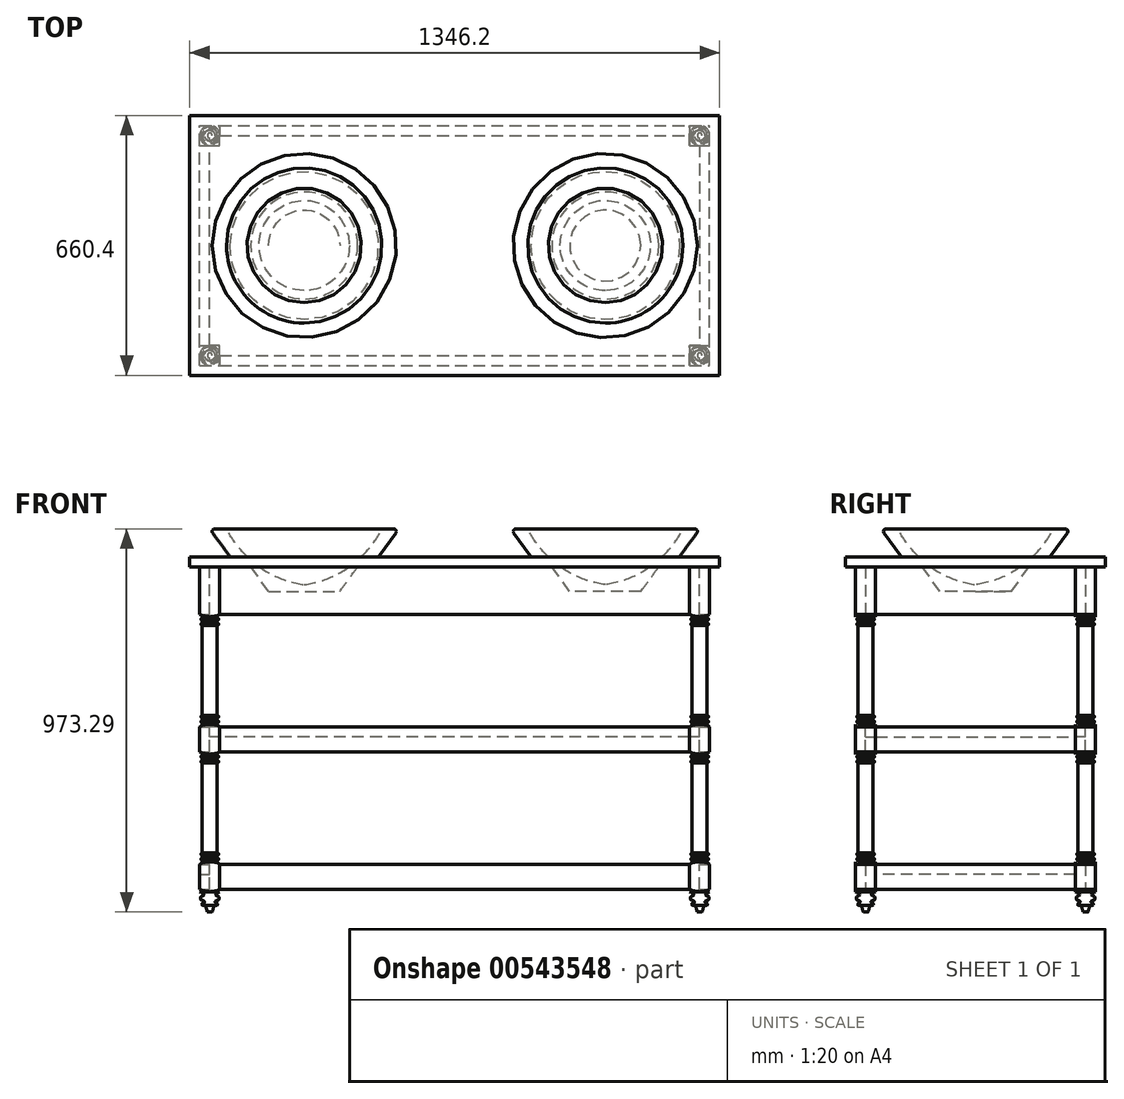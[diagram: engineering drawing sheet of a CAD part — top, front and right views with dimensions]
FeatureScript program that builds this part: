
annotation { "Feature Type Name" : "Feature", "Feature Type Description" : "" }
export const myFeature = defineFeature(function(context is Context, id is Id, definition is map)
    precondition{}
    {
        {
            var Q0;
            Q0=qCreatedBy(makeId("Front.planeOp"),FACE);
            var sketch = newSketch(context, id + "F0", { "sketchPlane" : qUnion([Q0])});
            skLineSegment(sketch, "E0", {"start": v(-464.69, 397.34) * mm, "end": v(-413.89, 397.34) * mm});
            skLineSegment(sketch, "E1", {"start": v(-464.69, 270.34) * mm, "end": v(-413.89, 270.34) * mm});
            skArc(sketch, "E2", {"start": v(-464.69, 276.7) * mm, "mid": v(-439.29, 270.34) * mm, "end": v(-413.89, 276.7) * mm});
            skArc(sketch, "E3", {"start": v(-458.34, 267.17) * mm, "mid": v(-461.51, 264) * mm, "end": v(-458.34, 260.82) * mm});
            skArc(sketch, "E4", {"start": v(-420.24, 260.82) * mm, "mid": v(-417.06, 264) * mm, "end": v(-420.24, 267.17) * mm});
            skArc(sketch, "E5", {"start": v(-458.34, 254.47) * mm, "mid": v(-461.51, 251.3) * mm, "end": v(-458.34, 248.12) * mm});
            skArc(sketch, "E6", {"start": v(-420.24, 248.12) * mm, "mid": v(-417.06, 251.3) * mm, "end": v(-420.24, 254.47) * mm});
            skLineSegment(sketch, "E7", {"start": v(-458.34, 267.17) * mm, "end": v(-458.34, 270.34) * mm});
            skLineSegment(sketch, "E8", {"start": v(-458.34, 260.82) * mm, "end": v(-458.34, 254.47) * mm});
            skLineSegment(sketch, "E9", {"start": v(-420.24, 267.17) * mm, "end": v(-420.24, 270.34) * mm});
            skLineSegment(sketch, "E10", {"start": v(-420.24, 260.82) * mm, "end": v(-420.24, 254.47) * mm});
            skLineSegment(sketch, "E11", {"start": v(-464.69, -2.7) * mm, "end": v(-413.89, -2.7) * mm});
            skArc(sketch, "E12", {"start": v(-413.89, -9.06) * mm, "mid": v(-439.29, -2.7) * mm, "end": v(-464.69, -9.06) * mm});
            skArc(sketch, "E13", {"start": v(-458.34, 6.82) * mm, "mid": v(-461.51, 3.64) * mm, "end": v(-458.34, 0.47) * mm});
            skArc(sketch, "E14", {"start": v(-420.24, 0.47) * mm, "mid": v(-417.06, 3.64) * mm, "end": v(-420.24, 6.82) * mm});
            skArc(sketch, "E15", {"start": v(-458.34, 19.52) * mm, "mid": v(-461.51, 16.34) * mm, "end": v(-458.34, 13.17) * mm});
            skArc(sketch, "E16", {"start": v(-420.24, 13.17) * mm, "mid": v(-417.06, 16.34) * mm, "end": v(-420.24, 19.52) * mm});
            skLineSegment(sketch, "E17", {"start": v(-458.34, 0.47) * mm, "end": v(-458.34, -2.7) * mm});
            skLineSegment(sketch, "E18", {"start": v(-458.34, 6.82) * mm, "end": v(-458.34, 13.17) * mm});
            skLineSegment(sketch, "E19", {"start": v(-420.24, 0.47) * mm, "end": v(-420.24, -2.7) * mm});
            skLineSegment(sketch, "E20", {"start": v(-420.24, 6.82) * mm, "end": v(-420.24, 13.17) * mm});
            skLineSegment(sketch, "E21", {"start": v(-458.34, 248.12) * mm, "end": v(-458.34, 19.52) * mm});
            skLineSegment(sketch, "E22", {"start": v(-420.24, 248.12) * mm, "end": v(-420.24, 19.52) * mm});
            skLineSegment(sketch, "E23", {"start": v(-464.69, -78.9) * mm, "end": v(-413.89, -78.9) * mm});
            skLineSegment(sketch, "E24", {"start": v(-464.69, -78.9) * mm, "end": v(-464.69, -2.7) * mm});
            skLineSegment(sketch, "E25", {"start": v(-413.89, -2.7) * mm, "end": v(-413.89, -78.9) * mm});
            skArc(sketch, "E26", {"start": v(-464.69, -72.56) * mm, "mid": v(-439.29, -78.9) * mm, "end": v(-413.89, -72.56) * mm});
            skArc(sketch, "E27", {"start": v(-458.34, -342.43) * mm, "mid": v(-461.51, -345.6) * mm, "end": v(-458.34, -348.78) * mm});
            skArc(sketch, "E28", {"start": v(-420.24, -348.78) * mm, "mid": v(-417.06, -345.6) * mm, "end": v(-420.24, -342.43) * mm});
            skArc(sketch, "E29", {"start": v(-458.34, -329.73) * mm, "mid": v(-461.51, -332.9) * mm, "end": v(-458.34, -336.08) * mm});
            skArc(sketch, "E30", {"start": v(-420.24, -336.08) * mm, "mid": v(-417.06, -332.9) * mm, "end": v(-420.24, -329.73) * mm});
            skLineSegment(sketch, "E31", {"start": v(-458.34, -342.43) * mm, "end": v(-458.34, -336.08) * mm});
            skLineSegment(sketch, "E32", {"start": v(-420.24, -342.43) * mm, "end": v(-420.24, -336.08) * mm});
            skArc(sketch, "E33", {"start": v(-458.34, -82.08) * mm, "mid": v(-461.51, -85.26) * mm, "end": v(-458.34, -88.43) * mm});
            skArc(sketch, "E34", {"start": v(-420.24, -88.43) * mm, "mid": v(-417.06, -85.26) * mm, "end": v(-420.24, -82.08) * mm});
            skArc(sketch, "E35", {"start": v(-458.34, -94.78) * mm, "mid": v(-461.51, -97.96) * mm, "end": v(-458.34, -101.13) * mm});
            skArc(sketch, "E36", {"start": v(-420.24, -101.13) * mm, "mid": v(-417.06, -97.96) * mm, "end": v(-420.24, -94.78) * mm});
            skLineSegment(sketch, "E37", {"start": v(-458.34, -88.43) * mm, "end": v(-458.34, -94.78) * mm});
            skLineSegment(sketch, "E38", {"start": v(-420.24, -88.43) * mm, "end": v(-420.24, -94.78) * mm});
            skLineSegment(sketch, "E39", {"start": v(-458.34, -329.73) * mm, "end": v(-458.34, -101.13) * mm});
            skLineSegment(sketch, "E40", {"start": v(-420.24, -329.73) * mm, "end": v(-420.24, -101.13) * mm});
            skLineSegment(sketch, "E41", {"start": v(-413.89, 397.34) * mm, "end": v(-413.89, 270.34) * mm});
            skLineSegment(sketch, "E42", {"start": v(-464.69, 270.34) * mm, "end": v(-464.69, 397.34) * mm});
            skLineSegment(sketch, "E43", {"start": v(-458.34, -82.08) * mm, "end": v(-458.34, -78.9) * mm});
            skLineSegment(sketch, "E44", {"start": v(-420.24, -82.08) * mm, "end": v(-420.24, -78.9) * mm});
            skLineSegment(sketch, "E45", {"start": v(-464.69, -428.16) * mm, "end": v(-413.89, -428.16) * mm});
            skArc(sketch, "E46", {"start": v(-464.69, -421.8) * mm, "mid": v(-439.29, -428.16) * mm, "end": v(-413.89, -421.8) * mm});
            skLineSegment(sketch, "E47", {"start": v(-464.69, -351.96) * mm, "end": v(-413.89, -351.96) * mm});
            skLineSegment(sketch, "E48", {"start": v(-464.69, -351.96) * mm, "end": v(-464.69, -428.16) * mm});
            skLineSegment(sketch, "E49", {"start": v(-413.89, -428.16) * mm, "end": v(-413.89, -351.96) * mm});
            skArc(sketch, "E50", {"start": v(-413.89, -358.3) * mm, "mid": v(-439.29, -351.96) * mm, "end": v(-464.69, -358.3) * mm});
            skLineSegment(sketch, "E51", {"start": v(-458.34, -348.78) * mm, "end": v(-458.34, -351.96) * mm});
            skLineSegment(sketch, "E52", {"start": v(-420.24, -348.78) * mm, "end": v(-420.24, -351.96) * mm});
            skFitSpline(sketch, "E53", {"points": [v(-464.69, -428.16) * mm, v(-457.34, -432.47) * mm, v(-454.04, -435.15) * mm, v(-455.28, -437.83) * mm, v(-459.6, -439.69) * mm, v(-462.5, -441.75) * mm, v(-463.11, -444.43) * mm, v(-462.7, -448.14) * mm, v(-460.02, -449.79) * mm, v(-456.72, -451.03) * mm, v(-454.66, -451.44) * mm, v(-452.6, -454.94) * mm, v(-455.9, -457.21) * mm, v(-459.2, -458.86) * mm, v(-459.4, -461.34) * mm, v(-457.54, -462.37) * mm, v(-455.9, -462.57) * mm, v(-453, -462.99) * mm]});
            skFitSpline(sketch, "E54", {"points": [v(-413.89, -428.16) * mm, v(-421.23, -432.47) * mm, v(-424.53, -435.15) * mm, v(-423.3, -437.83) * mm, v(-418.97, -439.69) * mm, v(-416.08, -441.75) * mm, v(-415.46, -444.43) * mm, v(-415.87, -448.14) * mm, v(-418.55, -449.79) * mm, v(-421.85, -451.03) * mm, v(-423.91, -451.44) * mm, v(-425.98, -454.94) * mm, v(-422.68, -457.21) * mm, v(-419.38, -458.86) * mm, v(-419.17, -461.34) * mm, v(-421.03, -462.37) * mm, v(-422.68, -462.57) * mm, v(-425.56, -462.99) * mm]});
            skLineSegment(sketch, "E55", {"start": v(-445.58, -479.9) * mm, "end": v(-432.99, -479.9) * mm});
            skLineSegment(sketch, "E56", {"start": v(779.91, 397.34) * mm, "end": v(830.71, 397.34) * mm});
            skLineSegment(sketch, "E57", {"start": v(779.91, 270.34) * mm, "end": v(830.71, 270.34) * mm});
            skArc(sketch, "E58", {"start": v(779.91, 276.7) * mm, "mid": v(805.31, 270.34) * mm, "end": v(830.71, 276.7) * mm});
            skArc(sketch, "E59", {"start": v(786.26, 267.17) * mm, "mid": v(783.09, 264) * mm, "end": v(786.26, 260.82) * mm});
            skArc(sketch, "E60", {"start": v(824.36, 260.82) * mm, "mid": v(827.54, 264) * mm, "end": v(824.36, 267.17) * mm});
            skArc(sketch, "E61", {"start": v(786.26, 254.47) * mm, "mid": v(783.09, 251.3) * mm, "end": v(786.26, 248.12) * mm});
            skArc(sketch, "E62", {"start": v(824.36, 248.12) * mm, "mid": v(827.54, 251.3) * mm, "end": v(824.36, 254.47) * mm});
            skLineSegment(sketch, "E63", {"start": v(786.26, 267.17) * mm, "end": v(786.26, 270.34) * mm});
            skLineSegment(sketch, "E64", {"start": v(786.26, 260.82) * mm, "end": v(786.26, 254.47) * mm});
            skLineSegment(sketch, "E65", {"start": v(824.36, 267.17) * mm, "end": v(824.36, 270.34) * mm});
            skLineSegment(sketch, "E66", {"start": v(824.36, 260.82) * mm, "end": v(824.36, 254.47) * mm});
            skLineSegment(sketch, "E67", {"start": v(779.91, -2.7) * mm, "end": v(830.71, -2.7) * mm});
            skArc(sketch, "E68", {"start": v(830.71, -9.06) * mm, "mid": v(805.31, -2.7) * mm, "end": v(779.91, -9.06) * mm});
            skArc(sketch, "E69", {"start": v(786.26, 6.82) * mm, "mid": v(783.09, 3.64) * mm, "end": v(786.26, 0.47) * mm});
            skArc(sketch, "E70", {"start": v(824.36, 0.47) * mm, "mid": v(827.54, 3.64) * mm, "end": v(824.36, 6.82) * mm});
            skArc(sketch, "E71", {"start": v(786.26, 19.52) * mm, "mid": v(783.09, 16.34) * mm, "end": v(786.26, 13.17) * mm});
            skArc(sketch, "E72", {"start": v(824.36, 13.17) * mm, "mid": v(827.54, 16.34) * mm, "end": v(824.36, 19.52) * mm});
            skLineSegment(sketch, "E73", {"start": v(786.26, 0.47) * mm, "end": v(786.26, -2.7) * mm});
            skLineSegment(sketch, "E74", {"start": v(786.26, 6.82) * mm, "end": v(786.26, 13.17) * mm});
            skLineSegment(sketch, "E75", {"start": v(824.36, 0.47) * mm, "end": v(824.36, -2.7) * mm});
            skLineSegment(sketch, "E76", {"start": v(824.36, 6.82) * mm, "end": v(824.36, 13.17) * mm});
            skLineSegment(sketch, "E77", {"start": v(786.26, 248.12) * mm, "end": v(786.26, 19.52) * mm});
            skLineSegment(sketch, "E78", {"start": v(824.36, 248.12) * mm, "end": v(824.36, 19.52) * mm});
            skLineSegment(sketch, "E79", {"start": v(779.91, -78.9) * mm, "end": v(830.71, -78.9) * mm});
            skLineSegment(sketch, "E80", {"start": v(779.91, -78.9) * mm, "end": v(779.91, -2.7) * mm});
            skLineSegment(sketch, "E81", {"start": v(830.71, -2.7) * mm, "end": v(830.71, -78.9) * mm});
            skArc(sketch, "E82", {"start": v(779.91, -72.56) * mm, "mid": v(805.31, -78.9) * mm, "end": v(830.71, -72.56) * mm});
            skArc(sketch, "E83", {"start": v(786.26, -342.43) * mm, "mid": v(783.09, -345.6) * mm, "end": v(786.26, -348.78) * mm});
            skArc(sketch, "E84", {"start": v(824.36, -348.78) * mm, "mid": v(827.54, -345.6) * mm, "end": v(824.36, -342.43) * mm});
            skArc(sketch, "E85", {"start": v(786.26, -329.73) * mm, "mid": v(783.09, -332.9) * mm, "end": v(786.26, -336.08) * mm});
            skArc(sketch, "E86", {"start": v(824.36, -336.08) * mm, "mid": v(827.54, -332.9) * mm, "end": v(824.36, -329.73) * mm});
            skLineSegment(sketch, "E87", {"start": v(786.26, -342.43) * mm, "end": v(786.26, -336.08) * mm});
            skLineSegment(sketch, "E88", {"start": v(824.36, -342.43) * mm, "end": v(824.36, -336.08) * mm});
            skArc(sketch, "E89", {"start": v(786.26, -82.08) * mm, "mid": v(783.09, -85.26) * mm, "end": v(786.26, -88.43) * mm});
            skArc(sketch, "E90", {"start": v(824.36, -88.43) * mm, "mid": v(827.54, -85.26) * mm, "end": v(824.36, -82.08) * mm});
            skArc(sketch, "E91", {"start": v(786.26, -94.78) * mm, "mid": v(783.09, -97.96) * mm, "end": v(786.26, -101.13) * mm});
            skArc(sketch, "E92", {"start": v(824.36, -101.13) * mm, "mid": v(827.54, -97.96) * mm, "end": v(824.36, -94.78) * mm});
            skLineSegment(sketch, "E93", {"start": v(786.26, -88.43) * mm, "end": v(786.26, -94.78) * mm});
            skLineSegment(sketch, "E94", {"start": v(824.36, -88.43) * mm, "end": v(824.36, -94.78) * mm});
            skLineSegment(sketch, "E95", {"start": v(786.26, -329.73) * mm, "end": v(786.26, -101.13) * mm});
            skLineSegment(sketch, "E96", {"start": v(824.36, -329.73) * mm, "end": v(824.36, -101.13) * mm});
            skLineSegment(sketch, "E97", {"start": v(830.71, 397.34) * mm, "end": v(830.71, 270.34) * mm});
            skLineSegment(sketch, "E98", {"start": v(779.91, 270.34) * mm, "end": v(779.91, 397.34) * mm});
            skLineSegment(sketch, "E99", {"start": v(786.26, -82.08) * mm, "end": v(786.26, -78.9) * mm});
            skLineSegment(sketch, "E100", {"start": v(824.36, -82.08) * mm, "end": v(824.36, -78.9) * mm});
            skLineSegment(sketch, "E101", {"start": v(805.31, -428.16) * mm, "end": v(779.91, -428.16) * mm});
            skArc(sketch, "E102", {"start": v(779.91, -421.8) * mm, "mid": v(805.31, -428.16) * mm, "end": v(830.71, -421.8) * mm});
            skLineSegment(sketch, "E103", {"start": v(779.91, -351.96) * mm, "end": v(830.71, -351.96) * mm});
            skLineSegment(sketch, "E104", {"start": v(779.91, -351.96) * mm, "end": v(779.91, -428.16) * mm});
            skLineSegment(sketch, "E105", {"start": v(830.71, -428.16) * mm, "end": v(830.71, -351.96) * mm});
            skArc(sketch, "E106", {"start": v(830.71, -358.3) * mm, "mid": v(805.31, -351.96) * mm, "end": v(779.91, -358.3) * mm});
            skLineSegment(sketch, "E107", {"start": v(786.26, -348.78) * mm, "end": v(786.26, -351.96) * mm});
            skLineSegment(sketch, "E108", {"start": v(824.36, -348.78) * mm, "end": v(824.36, -351.96) * mm});
            skFitSpline(sketch, "E109", {"points": [v(779.91, -428.16) * mm, v(787.26, -432.47) * mm, v(790.56, -435.15) * mm, v(789.32, -437.83) * mm, v(785, -439.69) * mm, v(782.1, -441.75) * mm, v(781.49, -444.43) * mm, v(781.9, -448.14) * mm, v(784.58, -449.79) * mm, v(787.88, -451.03) * mm, v(789.94, -451.44) * mm, v(792, -454.94) * mm, v(788.7, -457.21) * mm, v(785.4, -458.86) * mm, v(785.2, -461.34) * mm, v(787.06, -462.37) * mm, v(788.7, -462.57) * mm, v(791.6, -462.99) * mm]});
            skFitSpline(sketch, "E110", {"points": [v(830.71, -428.16) * mm, v(823.37, -432.47) * mm, v(820.07, -435.15) * mm, v(821.3, -437.83) * mm, v(825.63, -439.69) * mm, v(828.52, -441.75) * mm, v(829.14, -444.43) * mm, v(828.73, -448.14) * mm, v(826.05, -449.79) * mm, v(822.75, -451.03) * mm, v(820.69, -451.44) * mm, v(818.62, -454.94) * mm, v(821.92, -457.21) * mm, v(825.22, -458.86) * mm, v(825.43, -461.34) * mm, v(823.57, -462.37) * mm, v(821.92, -462.57) * mm, v(819.04, -462.99) * mm]});
            skFitSpline(sketch, "E111", {"points": [v(-425.56, -462.99) * mm, v(-428.05, -464.67) * mm, v(-432.99, -479.9) * mm], "startDerivative": vector(-8.41, -3.1) * mm, "endDerivative": vector(-6.66, -27.5) * mm});
            skFitSpline(sketch, "E112.MirrorCS", {"points": [v(-453, -462.99) * mm, v(-450.52, -464.67) * mm, v(-445.58, -479.9) * mm], "startDerivative": vector(8.41, -3.1) * mm, "endDerivative": vector(6.66, -27.5) * mm});
            skLineSegment(sketch, "E113", {"start": v(-413.89, 397.34) * mm, "end": v(779.91, 397.34) * mm});
            skLineSegment(sketch, "E114", {"start": v(183.01, 397.34) * mm, "end": v(183.01, 64.11) * mm});
            skFitSpline(sketch, "E115.MirrorCS", {"points": [v(791.6, -462.99) * mm, v(794.08, -464.67) * mm, v(799.02, -479.9) * mm], "startDerivative": vector(8.41, -3.1) * mm, "endDerivative": vector(6.66, -27.5) * mm});
            skFitSpline(sketch, "E116.MirrorCS", {"points": [v(819.04, -462.99) * mm, v(816.55, -464.67) * mm, v(811.61, -479.9) * mm], "startDerivative": vector(-8.41, -3.1) * mm, "endDerivative": vector(-6.66, -27.5) * mm});
            skLineSegment(sketch, "E117", {"start": v(799.02, -479.9) * mm, "end": v(805.31, -479.9) * mm});
            skLineSegment(sketch, "E118", {"start": v(805.31, -428.16) * mm, "end": v(805.31, -479.9) * mm});
            skLineSegment(sketch, "E119", {"start": v(-439.29, -428.16) * mm, "end": v(-439.29, -479.9) * mm});
            skLineSegment(sketch, "E120", {"start": v(-439.29, -78.9) * mm, "end": v(-439.29, -351.96) * mm});
            skLineSegment(sketch, "E121", {"start": v(-439.29, 270.34) * mm, "end": v(-439.29, -2.7) * mm});
            skLineSegment(sketch, "E122", {"start": v(805.31, 270.34) * mm, "end": v(805.31, -2.7) * mm});
            skLineSegment(sketch, "E123", {"start": v(805.31, -78.9) * mm, "end": v(805.31, -351.96) * mm});
            skSolve(sketch);
        }
        {
            var Q0;
            {var subQ1=sQuery(id+"F0.wireOp",EDGE,"E0");Q0=makeQuery(id+"F0.imprint","IMPRINT",FACE,{"disambiguationData":[TD([[makeQuery(id+"F0.imprint","IMPRINT",EDGE,{"derivedFrom":subQ1}),-1.0]])]});}
            extrude(context, id + "F1", {"entities" : qUnion([Q0]), "endBound" : BoundingType.SYMMETRIC, "depth" : 50.8 * mm, "offsetDistance" : 25.4 * mm});
        }
        {
            var Q0;
            {var subQ1=sQuery(id+"F0.wireOp",EDGE,"E56");Q0=makeQuery(id+"F0.imprint","IMPRINT",FACE,{"disambiguationData":[TD([[makeQuery(id+"F0.imprint","IMPRINT",EDGE,{"derivedFrom":subQ1}),-1.0]])]});}
            var Q1;
            {var subQ1=sQuery(id+"F0.wireOp",EDGE,"E12");var subQ6=sQuery(id+"F0.wireOp",EDGE,"E25");var subQ9=makeQuery(id+"F0.imprint","INTERSECT",VERTEX,{"derivedFrom":[subQ1,subQ6]});Q1=makeQuery(id+"F0.imprint","IMPRINT",FACE,{"disambiguationData":[TD([[makeQuery(id+"F0.imprint","IMPRINT",EDGE,{"disambiguationData":[TD([[subQ9,-1.0]])],"derivedFrom":subQ1}),1.0]])]});}
            var Q2;
            {var subQ1=sQuery(id+"F0.wireOp",EDGE,"E68");var subQ6=sQuery(id+"F0.wireOp",EDGE,"E81");var subQ9=makeQuery(id+"F0.imprint","INTERSECT",VERTEX,{"derivedFrom":[subQ1,subQ6]});Q2=makeQuery(id+"F0.imprint","IMPRINT",FACE,{"disambiguationData":[TD([[makeQuery(id+"F0.imprint","IMPRINT",EDGE,{"disambiguationData":[TD([[subQ9,-1.0]])],"derivedFrom":subQ1}),1.0]])]});}
            var Q3;
            {var subQ0=sQuery(id+"F0.wireOp",EDGE,"E48");var subQ1=sQuery(id+"F0.wireOp",EDGE,"E46");var subQ2=makeQuery(id+"F0.imprint","INTERSECT",VERTEX,{"derivedFrom":[subQ1,subQ0]});Q3=makeQuery(id+"F0.imprint","IMPRINT",FACE,{"disambiguationData":[TD([[makeQuery(id+"F0.imprint","IMPRINT",EDGE,{"disambiguationData":[TD([[subQ2,-1.0]])],"derivedFrom":subQ1}),1.0]])]});}
            var Q4;
            {var subQ0=sQuery(id+"F0.wireOp",EDGE,"E104");var subQ1=sQuery(id+"F0.wireOp",EDGE,"E102");var subQ2=makeQuery(id+"F0.imprint","INTERSECT",VERTEX,{"derivedFrom":[subQ1,subQ0]});Q4=makeQuery(id+"F0.imprint","IMPRINT",FACE,{"disambiguationData":[TD([[makeQuery(id+"F0.imprint","IMPRINT",EDGE,{"disambiguationData":[TD([[subQ2,-1.0]])],"derivedFrom":subQ1}),1.0]])]});}
            extrude(context, id + "F2", {"entities" : qUnion([Q0, Q1, Q2, Q3, Q4]), "endBound" : BoundingType.SYMMETRIC, "depth" : 50.8 * mm, "offsetDistance" : 25.4 * mm});
        }
        {
            var Q0;
            Q0=makeQuery(id+"F0.imprint","IMPRINT",FACE,{"disambiguationData":[TD([[makeQuery(id+"F0.imprint","IMPRINT",EDGE,{"derivedFrom":sQuery(id+"F0.wireOp",EDGE,"E27")}),1.0]])]});
            var Q1;
            Q1=makeQuery(id+"F0.imprint","IMPRINT",FACE,{"disambiguationData":[TD([[makeQuery(id+"F0.imprint","IMPRINT",EDGE,{"derivedFrom":sQuery(id+"F0.wireOp",EDGE,"E3")}),1.0]])]});
            var Q2;
            Q2=sQuery(id+"F0.wireOp",EDGE,"E120");
            revolve(context, id + "F3", {"entities" : qUnion([Q0, Q1]), "axis" : qUnion([Q2]), "revolveType" : RevolveType.FULL});
        }
        {
            var Q0;
            {var subQ1=sQuery(id+"F0.wireOp",EDGE,"E53");Q0=makeQuery(id+"F0.imprint","IMPRINT",FACE,{"disambiguationData":[TD([[makeQuery(id+"F0.imprint","IMPRINT",EDGE,{"derivedFrom":subQ1}),1.0]])]});}
            var Q1;
            Q1=sQuery(id+"F0.wireOp",EDGE,"E119");
            revolve(context, id + "F4", {"operationType" : NewBodyOperationType.ADD, "entities" : qUnion([Q0]), "axis" : qUnion([Q1]), "revolveType" : RevolveType.FULL});
        }
        {
            var Q0;
            Q0=makeQuery(id+"F0.imprint","IMPRINT",FACE,{"disambiguationData":[TD([[makeQuery(id+"F0.imprint","IMPRINT",EDGE,{"derivedFrom":sQuery(id+"F0.wireOp",EDGE,"E59")}),1.0]])]});
            var Q1;
            Q1=makeQuery(id+"F0.imprint","IMPRINT",FACE,{"disambiguationData":[TD([[makeQuery(id+"F0.imprint","IMPRINT",EDGE,{"derivedFrom":sQuery(id+"F0.wireOp",EDGE,"E83")}),1.0]])]});
            var Q2;
            Q2=sQuery(id+"F0.wireOp",EDGE,"E122");
            revolve(context, id + "F5", {"entities" : qUnion([Q0, Q1]), "axis" : qUnion([Q2]), "revolveType" : RevolveType.FULL});
        }
        {
            var Q0;
            Q0=makeQuery(id+"F0.imprint","IMPRINT",FACE,{"disambiguationData":[TD([[makeQuery(id+"F0.imprint","IMPRINT",EDGE,{"derivedFrom":sQuery(id+"F0.wireOp",EDGE,"E101")}),1.0]])]});
            var Q1;
            Q1=sQuery(id+"F0.wireOp",EDGE,"E123");
            revolve(context, id + "F6", {"operationType" : NewBodyOperationType.ADD, "entities" : qUnion([Q0]), "axis" : qUnion([Q1]), "revolveType" : RevolveType.FULL});
        }
        {
            var Q0;
            Q0=qCreatedBy(makeId("Front.planeOp"),FACE);
            cPlane(context, id + "F7", {"entities" : qUnion([Q0]), "cplaneType" : CPlaneType.OFFSET, "offset" : 25.4 * mm, "width" : 152.4 * mm, "height" : 152.4 * mm});
        }
        {
            var Q0;
            Q0=qCreatedBy(id+"F7.planeOp",FACE);
            var sketch = newSketch(context, id + "F8", { "sketchPlane" : qUnion([Q0])});
            skLineSegment(sketch, "E124.0.0", {"start": v(-464.69, 397.34) * mm, "end": v(-464.69, 276.7) * mm});
            skArc(sketch, "E124.0.1", {"start": v(-464.69, 276.7) * mm, "mid": v(-439.29, 270.34) * mm, "end": v(-413.89, 276.7) * mm});
            skLineSegment(sketch, "E124.0.2", {"start": v(-413.89, 276.7) * mm, "end": v(-413.89, 397.34) * mm});
            skLineSegment(sketch, "E124.0.3", {"start": v(-413.89, 397.34) * mm, "end": v(-464.69, 397.34) * mm});
            skLineSegment(sketch, "E125.0.0", {"start": v(779.91, 397.34) * mm, "end": v(779.91, 276.7) * mm});
            skArc(sketch, "E125.0.1", {"start": v(779.91, 276.7) * mm, "mid": v(805.31, 270.34) * mm, "end": v(830.71, 276.7) * mm});
            skLineSegment(sketch, "E125.0.2", {"start": v(830.71, 276.7) * mm, "end": v(830.71, 397.34) * mm});
            skLineSegment(sketch, "E125.0.3", {"start": v(830.71, 397.34) * mm, "end": v(779.91, 397.34) * mm});
            skLineSegment(sketch, "E126.bottom", {"start": v(-413.89, 397.34) * mm, "end": v(779.91, 397.34) * mm});
            skLineSegment(sketch, "E126.top", {"start": v(-413.89, 276.7) * mm, "end": v(779.91, 276.7) * mm});
            skLineSegment(sketch, "E126.left", {"start": v(-413.89, 397.34) * mm, "end": v(-413.89, 276.7) * mm});
            skArc(sketch, "E127.0.0", {"start": v(779.91, -72.56) * mm, "mid": v(805.31, -78.9) * mm, "end": v(830.71, -72.56) * mm});
            skLineSegment(sketch, "E127.0.1", {"start": v(830.71, -72.56) * mm, "end": v(830.71, -9.06) * mm});
            skArc(sketch, "E127.0.2", {"start": v(830.71, -9.06) * mm, "mid": v(805.31, -2.7) * mm, "end": v(779.91, -9.06) * mm});
            skLineSegment(sketch, "E127.0.3", {"start": v(779.91, -9.06) * mm, "end": v(779.91, -72.56) * mm});
            skArc(sketch, "E127.1.0", {"start": v(-464.69, -72.56) * mm, "mid": v(-439.29, -78.9) * mm, "end": v(-413.89, -72.56) * mm});
            skLineSegment(sketch, "E127.1.1", {"start": v(-413.89, -72.56) * mm, "end": v(-413.89, -9.06) * mm});
            skArc(sketch, "E127.1.2", {"start": v(-413.89, -9.06) * mm, "mid": v(-439.29, -2.7) * mm, "end": v(-464.69, -9.06) * mm});
            skLineSegment(sketch, "E127.1.3", {"start": v(-464.69, -9.06) * mm, "end": v(-464.69, -72.56) * mm});
            skLineSegment(sketch, "E128.bottom", {"start": v(-413.89, -9.06) * mm, "end": v(779.91, -9.06) * mm});
            skLineSegment(sketch, "E128.top", {"start": v(-413.89, -72.56) * mm, "end": v(779.91, -72.56) * mm});
            skLineSegment(sketch, "E128.left", {"start": v(-413.89, -9.06) * mm, "end": v(-413.89, -72.56) * mm});
            skLineSegment(sketch, "E129.0.0", {"start": v(-413.89, -421.8) * mm, "end": v(-413.89, -358.3) * mm});
            skArc(sketch, "E129.0.1", {"start": v(-413.89, -358.3) * mm, "mid": v(-439.29, -351.96) * mm, "end": v(-464.69, -358.3) * mm});
            skLineSegment(sketch, "E129.0.2", {"start": v(-464.69, -358.3) * mm, "end": v(-464.69, -421.8) * mm});
            skArc(sketch, "E129.0.3", {"start": v(-464.69, -421.8) * mm, "mid": v(-439.29, -428.16) * mm, "end": v(-413.89, -421.8) * mm});
            skLineSegment(sketch, "E129.1.0", {"start": v(830.71, -421.8) * mm, "end": v(830.71, -358.3) * mm});
            skArc(sketch, "E129.1.1", {"start": v(830.71, -358.3) * mm, "mid": v(805.31, -351.96) * mm, "end": v(779.91, -358.3) * mm});
            skLineSegment(sketch, "E129.1.2", {"start": v(779.91, -358.3) * mm, "end": v(779.91, -421.8) * mm});
            skArc(sketch, "E129.1.3", {"start": v(779.91, -421.8) * mm, "mid": v(805.31, -428.16) * mm, "end": v(830.71, -421.8) * mm});
            skLineSegment(sketch, "E130.bottom", {"start": v(-413.89, -358.3) * mm, "end": v(779.91, -358.3) * mm});
            skLineSegment(sketch, "E130.top", {"start": v(-413.89, -421.8) * mm, "end": v(779.91, -421.8) * mm});
            skLineSegment(sketch, "E130.left", {"start": v(-413.89, -358.3) * mm, "end": v(-413.89, -421.8) * mm});
            skSolve(sketch);
        }
        {
            var Q0;
            Q0=makeQuery(id+"F8.imprint","IMPRINT",FACE,{"disambiguationData":[TD([[makeQuery(id+"F8.imprint","IMPRINT",EDGE,{"derivedFrom":sQuery(id+"F8.wireOp",EDGE,"E126.bottom")}),-1.0]])]});
            extrude(context, id + "F9", {"entities" : qUnion([Q0]), "oppositeDirection" : true, "depth" : 25.4 * mm, "offsetDistance" : 25.4 * mm});
        }
        {
            var Q0;
            Q0=makeQuery(id+"F8.imprint","IMPRINT",FACE,{"disambiguationData":[TD([[makeQuery(id+"F8.imprint","IMPRINT",EDGE,{"derivedFrom":sQuery(id+"F8.wireOp",EDGE,"E128.bottom")}),-1.0]])]});
            var Q1;
            Q1=makeQuery(id+"F8.imprint","IMPRINT",FACE,{"disambiguationData":[TD([[makeQuery(id+"F8.imprint","IMPRINT",EDGE,{"derivedFrom":sQuery(id+"F8.wireOp",EDGE,"E130.bottom")}),-1.0]])]});
            extrude(context, id + "F10", {"entities" : qUnion([Q0, Q1]), "oppositeDirection" : true, "depth" : 25.4 * mm, "offsetDistance" : 25.4 * mm});
        }
        {
            var Q0;
            Q0=makeQuery(id+"F2.opExtrude","SWEPT_FACE",FACE,{"disambiguationData":[OSD([sQuery(id+"F0.wireOp",EDGE,"E97")])]});
            cPlane(context, id + "F11", {"entities" : qUnion([Q0]), "cplaneType" : CPlaneType.OFFSET, "offset" : 0 * mm, "width" : 152.4 * mm, "height" : 152.4 * mm});
        }
        {
            var Q0;
            Q0=qCreatedBy(id+"F11.planeOp",FACE);
            var sketch = newSketch(context, id + "F12", { "sketchPlane" : qUnion([Q0])});
            skLineSegment(sketch, "E131.0.0", {"start": v(25.4, 276.7) * mm, "end": v(25.4, 397.34) * mm});
            skLineSegment(sketch, "E131.0.1", {"start": v(25.4, 397.34) * mm, "end": v(-25.4, 397.34) * mm});
            skLineSegment(sketch, "E131.0.2", {"start": v(-25.4, 397.34) * mm, "end": v(-25.4, 276.7) * mm});
            skLineSegment(sketch, "E131.0.3", {"start": v(-25.4, 276.7) * mm, "end": v(25.4, 276.7) * mm});
            skLineSegment(sketch, "E132.bottom", {"start": v(25.4, 397.34) * mm, "end": v(533.4, 397.34) * mm});
            skLineSegment(sketch, "E132.top", {"start": v(25.4, 276.7) * mm, "end": v(533.4, 276.7) * mm});
            skLineSegment(sketch, "E132.left", {"start": v(25.4, 397.34) * mm, "end": v(25.4, 276.7) * mm});
            skLineSegment(sketch, "E132.right", {"start": v(533.4, 397.34) * mm, "end": v(533.4, 276.7) * mm});
            skLineSegment(sketch, "E133.0.0", {"start": v(25.4, -72.56) * mm, "end": v(25.4, -9.06) * mm});
            skLineSegment(sketch, "E133.0.1", {"start": v(25.4, -9.06) * mm, "end": v(-25.4, -9.06) * mm});
            skLineSegment(sketch, "E133.0.2", {"start": v(-25.4, -9.06) * mm, "end": v(-25.4, -72.56) * mm});
            skLineSegment(sketch, "E133.0.3", {"start": v(-25.4, -72.56) * mm, "end": v(25.4, -72.56) * mm});
            skLineSegment(sketch, "E134.bottom", {"start": v(25.4, -9.06) * mm, "end": v(533.4, -9.06) * mm});
            skLineSegment(sketch, "E134.top", {"start": v(25.4, -72.56) * mm, "end": v(533.4, -72.56) * mm});
            skLineSegment(sketch, "E134.left", {"start": v(25.4, -9.06) * mm, "end": v(25.4, -72.56) * mm});
            skLineSegment(sketch, "E134.right", {"start": v(533.4, -9.06) * mm, "end": v(533.4, -72.56) * mm});
            skLineSegment(sketch, "E135.0.0", {"start": v(25.4, -421.8) * mm, "end": v(25.4, -358.3) * mm});
            skLineSegment(sketch, "E135.0.1", {"start": v(25.4, -358.3) * mm, "end": v(-25.4, -358.3) * mm});
            skLineSegment(sketch, "E135.0.2", {"start": v(-25.4, -358.3) * mm, "end": v(-25.4, -421.8) * mm});
            skLineSegment(sketch, "E135.0.3", {"start": v(-25.4, -421.8) * mm, "end": v(25.4, -421.8) * mm});
            skLineSegment(sketch, "E136.bottom", {"start": v(25.4, -358.3) * mm, "end": v(533.4, -358.3) * mm});
            skLineSegment(sketch, "E136.top", {"start": v(25.4, -421.8) * mm, "end": v(533.4, -421.8) * mm});
            skLineSegment(sketch, "E136.left", {"start": v(25.4, -358.3) * mm, "end": v(25.4, -421.8) * mm});
            skLineSegment(sketch, "E136.right", {"start": v(533.4, -358.3) * mm, "end": v(533.4, -421.8) * mm});
            skSolve(sketch);
        }
        {
            var Q0;
            Q0=makeQuery(id+"F12.imprint","IMPRINT",FACE,{"disambiguationData":[TD([[makeQuery(id+"F12.imprint","IMPRINT",EDGE,{"derivedFrom":sQuery(id+"F12.wireOp",EDGE,"E132.bottom")}),-1.0]])]});
            var Q1;
            Q1=makeQuery(id+"F12.imprint","IMPRINT",FACE,{"disambiguationData":[TD([[makeQuery(id+"F12.imprint","IMPRINT",EDGE,{"derivedFrom":sQuery(id+"F12.wireOp",EDGE,"E134.bottom")}),-1.0]])]});
            var Q2;
            Q2=makeQuery(id+"F12.imprint","IMPRINT",FACE,{"disambiguationData":[TD([[makeQuery(id+"F12.imprint","IMPRINT",EDGE,{"derivedFrom":sQuery(id+"F12.wireOp",EDGE,"E136.bottom")}),-1.0]])]});
            extrude(context, id + "F13", {"entities" : qUnion([Q0, Q1, Q2]), "oppositeDirection" : true, "depth" : 25.4 * mm, "offsetDistance" : 25.4 * mm});
        }
        {
            var Q0;
            Q0=makeQuery(id+"F13.opExtrude","SWEPT_BODY",BODY,{"disambiguationData":[OSD([sQuery(id+"F12.wireOp",EDGE,"E132.bottom"),sQuery(id+"F12.wireOp",EDGE,"E132.top"),sQuery(id+"F12.wireOp",EDGE,"E132.left"),sQuery(id+"F12.wireOp",EDGE,"E132.right")])]});
            transform(context, id + "F14", {"entities" : qUnion([Q0]), "transformType" : TransformType.TRANSLATION_3D, "dx" : -1270 * mm, "dy" : 0 * mm, "dz" : 0 * mm, "makeCopy" : true});
        }
        {
            var Q0;
            Q0=makeQuery(id+"F13.opExtrude","SWEPT_BODY",BODY,{"disambiguationData":[OSD([sQuery(id+"F12.wireOp",EDGE,"E134.bottom"),sQuery(id+"F12.wireOp",EDGE,"E134.top"),sQuery(id+"F12.wireOp",EDGE,"E134.left"),sQuery(id+"F12.wireOp",EDGE,"E134.right")])]});
            transform(context, id + "F15", {"entities" : qUnion([Q0]), "transformType" : TransformType.TRANSLATION_3D, "dx" : -1270 * mm, "dy" : 0 * mm, "dz" : 0 * mm, "makeCopy" : true});
        }
        {
            var Q0;
            Q0=makeQuery(id+"F13.opExtrude","SWEPT_BODY",BODY,{"disambiguationData":[OSD([sQuery(id+"F12.wireOp",EDGE,"E136.bottom"),sQuery(id+"F12.wireOp",EDGE,"E136.top"),sQuery(id+"F12.wireOp",EDGE,"E136.left"),sQuery(id+"F12.wireOp",EDGE,"E136.right")])]});
            transform(context, id + "F16", {"entities" : qUnion([Q0]), "transformType" : TransformType.TRANSLATION_3D, "dx" : -1270 * mm, "dy" : 0 * mm, "dz" : 0 * mm, "makeCopy" : true});
        }
        {
            var Q0;
            Q0=makeQuery(id+"F1.opExtrude","SWEPT_BODY",BODY,{"disambiguationData":[OSD([sQuery(id+"F0.wireOp",EDGE,"E0"),sQuery(id+"F0.wireOp",EDGE,"E2"),sQuery(id+"F0.wireOp",EDGE,"E41"),sQuery(id+"F0.wireOp",EDGE,"E42")])]});
            var Q1;
            Q1=makeQuery(id+"F2.opExtrude","SWEPT_BODY",BODY,{"disambiguationData":[OSD([sQuery(id+"F0.wireOp",EDGE,"E12"),sQuery(id+"F0.wireOp",EDGE,"E24"),sQuery(id+"F0.wireOp",EDGE,"E25"),sQuery(id+"F0.wireOp",EDGE,"E26")])]});
            var Q2;
            Q2=makeQuery(id+"F2.opExtrude","SWEPT_BODY",BODY,{"disambiguationData":[OSD([sQuery(id+"F0.wireOp",EDGE,"E46"),sQuery(id+"F0.wireOp",EDGE,"E48"),sQuery(id+"F0.wireOp",EDGE,"E49"),sQuery(id+"F0.wireOp",EDGE,"E50")])]});
            var Q3;
            Q3=makeQuery(id+"F3.opRevolve","SWEPT_BODY",BODY,{"disambiguationData":[OSD([sQuery(id+"F0.wireOp",EDGE,"E1"),sQuery(id+"F0.wireOp",EDGE,"E3"),sQuery(id+"F0.wireOp",EDGE,"E5"),sQuery(id+"F0.wireOp",EDGE,"E7"),sQuery(id+"F0.wireOp",EDGE,"E8"),sQuery(id+"F0.wireOp",EDGE,"E11"),sQuery(id+"F0.wireOp",EDGE,"E13"),sQuery(id+"F0.wireOp",EDGE,"E15"),sQuery(id+"F0.wireOp",EDGE,"E17"),sQuery(id+"F0.wireOp",EDGE,"E18"),sQuery(id+"F0.wireOp",EDGE,"E21"),sQuery(id+"F0.wireOp",EDGE,"E121")])]});
            var Q4;
            Q4=makeQuery(id+"F3.opRevolve","SWEPT_BODY",BODY,{"disambiguationData":[OSD([sQuery(id+"F0.wireOp",EDGE,"E23"),sQuery(id+"F0.wireOp",EDGE,"E27"),sQuery(id+"F0.wireOp",EDGE,"E29"),sQuery(id+"F0.wireOp",EDGE,"E31"),sQuery(id+"F0.wireOp",EDGE,"E33"),sQuery(id+"F0.wireOp",EDGE,"E35"),sQuery(id+"F0.wireOp",EDGE,"E37"),sQuery(id+"F0.wireOp",EDGE,"E39"),sQuery(id+"F0.wireOp",EDGE,"E43"),sQuery(id+"F0.wireOp",EDGE,"E47"),sQuery(id+"F0.wireOp",EDGE,"E51"),sQuery(id+"F0.wireOp",EDGE,"E120")])]});
            var Q5;
            Q5=makeQuery(id+"F4.opRevolve","SWEPT_BODY",BODY,{"disambiguationData":[OSD([sQuery(id+"F0.wireOp",EDGE,"E45"),sQuery(id+"F0.wireOp",EDGE,"E53"),sQuery(id+"F0.wireOp",EDGE,"E55"),sQuery(id+"F0.wireOp",EDGE,"E112.MirrorCS"),sQuery(id+"F0.wireOp",EDGE,"E119")])]});
            transform(context, id + "F17", {"entities" : qUnion([Q0, Q1, Q2, Q3, Q4, Q5]), "transformType" : TransformType.TRANSLATION_3D, "dx" : 0 * mm, "dy" : 508 * mm, "dz" : 0 * mm, "makeCopy" : true});
        }
        {
            var Q0;
            Q0=makeQuery(id+"F2.opExtrude","SWEPT_BODY",BODY,{"disambiguationData":[OSD([sQuery(id+"F0.wireOp",EDGE,"E56"),sQuery(id+"F0.wireOp",EDGE,"E58"),sQuery(id+"F0.wireOp",EDGE,"E97"),sQuery(id+"F0.wireOp",EDGE,"E98")])]});
            var Q1;
            Q1=makeQuery(id+"F2.opExtrude","SWEPT_BODY",BODY,{"disambiguationData":[OSD([sQuery(id+"F0.wireOp",EDGE,"E68"),sQuery(id+"F0.wireOp",EDGE,"E80"),sQuery(id+"F0.wireOp",EDGE,"E81"),sQuery(id+"F0.wireOp",EDGE,"E82")])]});
            var Q2;
            Q2=makeQuery(id+"F2.opExtrude","SWEPT_BODY",BODY,{"disambiguationData":[OSD([sQuery(id+"F0.wireOp",EDGE,"E102"),sQuery(id+"F0.wireOp",EDGE,"E104"),sQuery(id+"F0.wireOp",EDGE,"E105"),sQuery(id+"F0.wireOp",EDGE,"E106")])]});
            var Q3;
            Q3=makeQuery(id+"F5.opRevolve","SWEPT_BODY",BODY,{"disambiguationData":[OSD([sQuery(id+"F0.wireOp",EDGE,"E79"),sQuery(id+"F0.wireOp",EDGE,"E83"),sQuery(id+"F0.wireOp",EDGE,"E85"),sQuery(id+"F0.wireOp",EDGE,"E87"),sQuery(id+"F0.wireOp",EDGE,"E89"),sQuery(id+"F0.wireOp",EDGE,"E91"),sQuery(id+"F0.wireOp",EDGE,"E93"),sQuery(id+"F0.wireOp",EDGE,"E95"),sQuery(id+"F0.wireOp",EDGE,"E99"),sQuery(id+"F0.wireOp",EDGE,"E103"),sQuery(id+"F0.wireOp",EDGE,"E107"),sQuery(id+"F0.wireOp",EDGE,"E123")])]});
            var Q4;
            Q4=makeQuery(id+"F5.opRevolve","SWEPT_BODY",BODY,{"disambiguationData":[OSD([sQuery(id+"F0.wireOp",EDGE,"E57"),sQuery(id+"F0.wireOp",EDGE,"E59"),sQuery(id+"F0.wireOp",EDGE,"E61"),sQuery(id+"F0.wireOp",EDGE,"E63"),sQuery(id+"F0.wireOp",EDGE,"E64"),sQuery(id+"F0.wireOp",EDGE,"E67"),sQuery(id+"F0.wireOp",EDGE,"E69"),sQuery(id+"F0.wireOp",EDGE,"E71"),sQuery(id+"F0.wireOp",EDGE,"E73"),sQuery(id+"F0.wireOp",EDGE,"E74"),sQuery(id+"F0.wireOp",EDGE,"E77"),sQuery(id+"F0.wireOp",EDGE,"E122")])]});
            var Q5;
            Q5=makeQuery(id+"F6.opRevolve","SWEPT_BODY",BODY,{"disambiguationData":[OSD([sQuery(id+"F0.wireOp",EDGE,"E101"),sQuery(id+"F0.wireOp",EDGE,"E109"),sQuery(id+"F0.wireOp",EDGE,"E115.MirrorCS"),sQuery(id+"F0.wireOp",EDGE,"E117"),sQuery(id+"F0.wireOp",EDGE,"E118")])]});
            transform(context, id + "F18", {"entities" : qUnion([Q0, Q1, Q2, Q3, Q4, Q5]), "transformType" : TransformType.TRANSLATION_3D, "dx" : 0 * mm, "dy" : 508 * mm, "dz" : 0 * mm, "makeCopy" : true});
        }
        {
            var Q0;
            Q0=makeQuery(id+"F10.opExtrude","SWEPT_BODY",BODY,{"disambiguationData":[OSD([sQuery(id+"F8.wireOp",EDGE,"E130.bottom"),sQuery(id+"F8.wireOp",EDGE,"E130.top"),sQuery(id+"F8.wireOp",EDGE,"E130.left"),sQuery(id+"F8.wireOp",EDGE,"E129.1.2")])]});
            var Q1;
            Q1=makeQuery(id+"F10.opExtrude","SWEPT_BODY",BODY,{"disambiguationData":[OSD([sQuery(id+"F8.wireOp",EDGE,"E128.bottom"),sQuery(id+"F8.wireOp",EDGE,"E128.top"),sQuery(id+"F8.wireOp",EDGE,"E128.left"),sQuery(id+"F8.wireOp",EDGE,"E127.0.3")])]});
            var Q2;
            Q2=makeQuery(id+"F9.opExtrude","SWEPT_BODY",BODY,{"disambiguationData":[OSD([sQuery(id+"F8.wireOp",EDGE,"E126.bottom"),sQuery(id+"F8.wireOp",EDGE,"E126.top"),sQuery(id+"F8.wireOp",EDGE,"E126.left"),sQuery(id+"F8.wireOp",EDGE,"E125.0.0")])]});
            transform(context, id + "F19", {"entities" : qUnion([Q0, Q1, Q2]), "transformType" : TransformType.TRANSLATION_3D, "dx" : 0 * mm, "dy" : 533.4 * mm, "dz" : 0 * mm, "makeCopy" : true});
        }
        {
            var Q0;
            Q0=makeQuery(id+"F17.opPattern","COPY",BODY,{"derivedFrom":makeQuery(id+"F1.opExtrude","SWEPT_BODY",BODY,{"disambiguationData":[OSD([sQuery(id+"F0.wireOp",EDGE,"E0"),sQuery(id+"F0.wireOp",EDGE,"E2"),sQuery(id+"F0.wireOp",EDGE,"E41"),sQuery(id+"F0.wireOp",EDGE,"E42")])]}),"instanceName":"1"});
            var Q1;
            Q1=makeQuery(id+"F17.opPattern","COPY",BODY,{"derivedFrom":makeQuery(id+"F2.opExtrude","SWEPT_BODY",BODY,{"disambiguationData":[OSD([sQuery(id+"F0.wireOp",EDGE,"E12"),sQuery(id+"F0.wireOp",EDGE,"E24"),sQuery(id+"F0.wireOp",EDGE,"E25"),sQuery(id+"F0.wireOp",EDGE,"E26")])]}),"instanceName":"1"});
            var Q2;
            Q2=makeQuery(id+"F17.opPattern","COPY",BODY,{"derivedFrom":makeQuery(id+"F2.opExtrude","SWEPT_BODY",BODY,{"disambiguationData":[OSD([sQuery(id+"F0.wireOp",EDGE,"E46"),sQuery(id+"F0.wireOp",EDGE,"E48"),sQuery(id+"F0.wireOp",EDGE,"E49"),sQuery(id+"F0.wireOp",EDGE,"E50")])]}),"instanceName":"1"});
            var Q3;
            Q3=makeQuery(id+"F17.opPattern","COPY",BODY,{"derivedFrom":makeQuery(id+"F3.opRevolve","SWEPT_BODY",BODY,{"disambiguationData":[OSD([sQuery(id+"F0.wireOp",EDGE,"E1"),sQuery(id+"F0.wireOp",EDGE,"E3"),sQuery(id+"F0.wireOp",EDGE,"E5"),sQuery(id+"F0.wireOp",EDGE,"E7"),sQuery(id+"F0.wireOp",EDGE,"E8"),sQuery(id+"F0.wireOp",EDGE,"E11"),sQuery(id+"F0.wireOp",EDGE,"E13"),sQuery(id+"F0.wireOp",EDGE,"E15"),sQuery(id+"F0.wireOp",EDGE,"E17"),sQuery(id+"F0.wireOp",EDGE,"E18"),sQuery(id+"F0.wireOp",EDGE,"E21"),sQuery(id+"F0.wireOp",EDGE,"E121")])]}),"instanceName":"1"});
            var Q4;
            Q4=makeQuery(id+"F17.opPattern","COPY",BODY,{"derivedFrom":makeQuery(id+"F3.opRevolve","SWEPT_BODY",BODY,{"disambiguationData":[OSD([sQuery(id+"F0.wireOp",EDGE,"E23"),sQuery(id+"F0.wireOp",EDGE,"E27"),sQuery(id+"F0.wireOp",EDGE,"E29"),sQuery(id+"F0.wireOp",EDGE,"E31"),sQuery(id+"F0.wireOp",EDGE,"E33"),sQuery(id+"F0.wireOp",EDGE,"E35"),sQuery(id+"F0.wireOp",EDGE,"E37"),sQuery(id+"F0.wireOp",EDGE,"E39"),sQuery(id+"F0.wireOp",EDGE,"E43"),sQuery(id+"F0.wireOp",EDGE,"E47"),sQuery(id+"F0.wireOp",EDGE,"E51"),sQuery(id+"F0.wireOp",EDGE,"E120")])]}),"instanceName":"1"});
            var Q5;
            Q5=makeQuery(id+"F17.opPattern","COPY",BODY,{"derivedFrom":makeQuery(id+"F4.opRevolve","SWEPT_BODY",BODY,{"disambiguationData":[OSD([sQuery(id+"F0.wireOp",EDGE,"E45"),sQuery(id+"F0.wireOp",EDGE,"E53"),sQuery(id+"F0.wireOp",EDGE,"E55"),sQuery(id+"F0.wireOp",EDGE,"E112.MirrorCS"),sQuery(id+"F0.wireOp",EDGE,"E119")])]}),"instanceName":"1"});
            var Q6;
            Q6=makeQuery(id+"F18.opPattern","COPY",BODY,{"derivedFrom":makeQuery(id+"F2.opExtrude","SWEPT_BODY",BODY,{"disambiguationData":[OSD([sQuery(id+"F0.wireOp",EDGE,"E56"),sQuery(id+"F0.wireOp",EDGE,"E58"),sQuery(id+"F0.wireOp",EDGE,"E97"),sQuery(id+"F0.wireOp",EDGE,"E98")])]}),"instanceName":"1"});
            var Q7;
            Q7=makeQuery(id+"F18.opPattern","COPY",BODY,{"derivedFrom":makeQuery(id+"F2.opExtrude","SWEPT_BODY",BODY,{"disambiguationData":[OSD([sQuery(id+"F0.wireOp",EDGE,"E68"),sQuery(id+"F0.wireOp",EDGE,"E80"),sQuery(id+"F0.wireOp",EDGE,"E81"),sQuery(id+"F0.wireOp",EDGE,"E82")])]}),"instanceName":"1"});
            var Q8;
            Q8=makeQuery(id+"F18.opPattern","COPY",BODY,{"derivedFrom":makeQuery(id+"F2.opExtrude","SWEPT_BODY",BODY,{"disambiguationData":[OSD([sQuery(id+"F0.wireOp",EDGE,"E102"),sQuery(id+"F0.wireOp",EDGE,"E104"),sQuery(id+"F0.wireOp",EDGE,"E105"),sQuery(id+"F0.wireOp",EDGE,"E106")])]}),"instanceName":"1"});
            var Q9;
            Q9=makeQuery(id+"F18.opPattern","COPY",BODY,{"derivedFrom":makeQuery(id+"F5.opRevolve","SWEPT_BODY",BODY,{"disambiguationData":[OSD([sQuery(id+"F0.wireOp",EDGE,"E57"),sQuery(id+"F0.wireOp",EDGE,"E59"),sQuery(id+"F0.wireOp",EDGE,"E61"),sQuery(id+"F0.wireOp",EDGE,"E63"),sQuery(id+"F0.wireOp",EDGE,"E64"),sQuery(id+"F0.wireOp",EDGE,"E67"),sQuery(id+"F0.wireOp",EDGE,"E69"),sQuery(id+"F0.wireOp",EDGE,"E71"),sQuery(id+"F0.wireOp",EDGE,"E73"),sQuery(id+"F0.wireOp",EDGE,"E74"),sQuery(id+"F0.wireOp",EDGE,"E77"),sQuery(id+"F0.wireOp",EDGE,"E122")])]}),"instanceName":"1"});
            var Q10;
            Q10=makeQuery(id+"F18.opPattern","COPY",BODY,{"derivedFrom":makeQuery(id+"F5.opRevolve","SWEPT_BODY",BODY,{"disambiguationData":[OSD([sQuery(id+"F0.wireOp",EDGE,"E79"),sQuery(id+"F0.wireOp",EDGE,"E83"),sQuery(id+"F0.wireOp",EDGE,"E85"),sQuery(id+"F0.wireOp",EDGE,"E87"),sQuery(id+"F0.wireOp",EDGE,"E89"),sQuery(id+"F0.wireOp",EDGE,"E91"),sQuery(id+"F0.wireOp",EDGE,"E93"),sQuery(id+"F0.wireOp",EDGE,"E95"),sQuery(id+"F0.wireOp",EDGE,"E99"),sQuery(id+"F0.wireOp",EDGE,"E103"),sQuery(id+"F0.wireOp",EDGE,"E107"),sQuery(id+"F0.wireOp",EDGE,"E123")])]}),"instanceName":"1"});
            var Q11;
            Q11=makeQuery(id+"F18.opPattern","COPY",BODY,{"derivedFrom":makeQuery(id+"F6.opRevolve","SWEPT_BODY",BODY,{"disambiguationData":[OSD([sQuery(id+"F0.wireOp",EDGE,"E101"),sQuery(id+"F0.wireOp",EDGE,"E109"),sQuery(id+"F0.wireOp",EDGE,"E115.MirrorCS"),sQuery(id+"F0.wireOp",EDGE,"E117"),sQuery(id+"F0.wireOp",EDGE,"E118")])]}),"instanceName":"1"});
            var Q12;
            Q12=makeQuery(id+"F19.opPattern","COPY",BODY,{"derivedFrom":makeQuery(id+"F9.opExtrude","SWEPT_BODY",BODY,{"disambiguationData":[OSD([sQuery(id+"F8.wireOp",EDGE,"E126.bottom"),sQuery(id+"F8.wireOp",EDGE,"E126.top"),sQuery(id+"F8.wireOp",EDGE,"E126.left"),sQuery(id+"F8.wireOp",EDGE,"E125.0.0")])]}),"instanceName":"1"});
            var Q13;
            Q13=makeQuery(id+"F19.opPattern","COPY",BODY,{"derivedFrom":makeQuery(id+"F10.opExtrude","SWEPT_BODY",BODY,{"disambiguationData":[OSD([sQuery(id+"F8.wireOp",EDGE,"E128.bottom"),sQuery(id+"F8.wireOp",EDGE,"E128.top"),sQuery(id+"F8.wireOp",EDGE,"E128.left"),sQuery(id+"F8.wireOp",EDGE,"E127.0.3")])]}),"instanceName":"1"});
            var Q14;
            Q14=makeQuery(id+"F19.opPattern","COPY",BODY,{"derivedFrom":makeQuery(id+"F10.opExtrude","SWEPT_BODY",BODY,{"disambiguationData":[OSD([sQuery(id+"F8.wireOp",EDGE,"E130.bottom"),sQuery(id+"F8.wireOp",EDGE,"E130.top"),sQuery(id+"F8.wireOp",EDGE,"E130.left"),sQuery(id+"F8.wireOp",EDGE,"E129.1.2")])]}),"instanceName":"1"});
            transform(context, id + "F20", {"entities" : qUnion([Q0, Q1, Q2, Q3, Q4, Q5, Q6, Q7, Q8, Q9, Q10, Q11, Q12, Q13, Q14]), "transformType" : TransformType.TRANSLATION_3D, "dx" : 0 * mm, "dy" : 50.8 * mm, "dz" : 0 * mm, "makeCopy" : false});
        }
        {
            var Q0;
            Q0=makeQuery(id+"F17.opPattern","COPY",FACE,{"derivedFrom":makeQuery(id+"F1.opExtrude","SWEPT_FACE",FACE,{"disambiguationData":[OSD([sQuery(id+"F0.wireOp",EDGE,"E0")])]}),"instanceName":"1"});
            var sketch = newSketch(context, id + "F21", { "sketchPlane" : qUnion([Q0])});
            skLineSegment(sketch, "E137", {"start": v(-464.69, 584.2) * mm, "end": v(-464.69, 609.6) * mm});
            skLineSegment(sketch, "E138", {"start": v(-464.69, 609.6) * mm, "end": v(-490.09, 609.6) * mm});
            skLineSegment(sketch, "E139", {"start": v(830.71, -25.4) * mm, "end": v(856.11, -25.4) * mm});
            skLineSegment(sketch, "E140", {"start": v(856.11, -50.8) * mm, "end": v(856.11, -25.4) * mm});
            skLineSegment(sketch, "E141.bottom", {"start": v(-490.09, 609.6) * mm, "end": v(856.11, 609.6) * mm});
            skLineSegment(sketch, "E141.top", {"start": v(-490.09, -50.8) * mm, "end": v(856.11, -50.8) * mm});
            skLineSegment(sketch, "E141.left", {"start": v(-490.09, 609.6) * mm, "end": v(-490.09, -50.8) * mm});
            skLineSegment(sketch, "E141.right", {"start": v(856.11, 609.6) * mm, "end": v(856.11, -50.8) * mm});
            skLineSegment(sketch, "E142", {"start": v(-464.69, 279.4) * mm, "end": v(830.71, 279.4) * mm});
            skLineSegment(sketch, "E143.0", {"start": v(-464.69, 25.4) * mm, "end": v(-464.69, 533.4) * mm});
            skLineSegment(sketch, "E144.0", {"start": v(830.71, 25.4) * mm, "end": v(830.71, 533.4) * mm});
            skPoint(sketch, "E145.orphan", {"position": v(856.11, 279.4) * mm});
            skPoint(sketch, "E146.orphan", {"position": v(-490.09, 279.4) * mm});
            skSolve(sketch);
        }
        {
            var Q0;
            {var subQ1=sQuery(id+"F21.wireOp",EDGE,"E141.top");Q0=makeQuery(id+"F21.imprint","IMPRINT",FACE,{"disambiguationData":[TD([[makeQuery(id+"F21.imprint","IMPRINT",EDGE,{"derivedFrom":subQ1}),1.0]])]});}
            var Q1;
            {var subQ0=sQuery(id+"F0.wireOp",EDGE,"E0");Q1=makeQuery(id+"F21.imprint","IMPRINT",FACE,{"disambiguationData":[TD([[makeQuery(id+"F21.imprint","IMPRINT",EDGE,{"derivedFrom":makeQuery(id+"F17.opPattern","COPY",EDGE,{"derivedFrom":makeQuery(id+"F1.opExtrude","CAP_EDGE",EDGE,{"disambiguationData":[OSD([subQ0])],"isStart":true}),"instanceName":"1"})}),-1.0]])]});}
            extrude(context, id + "F22", {"entities" : qUnion([Q0, Q1]), "depth" : 25.4 * mm, "offsetDistance" : 25.4 * mm});
        }
        {
            var Q0;
            Q0=qCreatedBy(id+"F7.planeOp",FACE);
            cPlane(context, id + "F23", {"entities" : qUnion([Q0]), "cplaneType" : CPlaneType.OFFSET, "offset" : 304.8 * mm, "oppositeDirection" : true, "width" : 152.4 * mm, "height" : 152.4 * mm});
        }
        {
            var Q0;
            Q0=qCreatedBy(id+"F23.planeOp",FACE);
            var sketch = newSketch(context, id + "F24", { "sketchPlane" : qUnion([Q0])});
            skLineSegment(sketch, "E147", {"start": v(-221.27, 483.32) * mm, "end": v(-179.63, 426.06) * mm});
            skLineSegment(sketch, "E148", {"start": v(-149.65, 415.28) * mm, "end": v(-159.92, 415.62) * mm});
            skLineSegment(sketch, "E149", {"start": v(-129.94, 404.83) * mm, "end": v(-79.05, 334.86) * mm});
            skLineSegment(sketch, "E150", {"start": v(11.4, 334.86) * mm, "end": v(11.4, 493.4) * mm});
            skLineSegment(sketch, "E151", {"start": v(-216.13, 493.4) * mm, "end": v(11.4, 493.4) * mm});
            skLineSegment(sketch, "E152", {"start": v(-79.05, 334.86) * mm, "end": v(11.4, 334.86) * mm});
            skLineSegment(sketch, "E153.filletArc", {"start": v(-92.34, 349.97) * mm, "end": v(-92.34, 349.97) * mm});
            skPoint(sketch, "E154.visualSharp", {"position": v(-228.6, 493.4) * mm});
            skArc(sketch, "E154.filletArc", {"start": v(-216.13, 493.4) * mm, "mid": v(-221.79, 489.94) * mm, "end": v(-221.27, 483.32) * mm});
            skPoint(sketch, "E155.visualSharp", {"position": v(-172.32, 416.03) * mm});
            skArc(sketch, "E155.filletArc", {"start": v(-179.63, 426.06) * mm, "mid": v(-170.98, 418.56) * mm, "end": v(-159.92, 415.62) * mm});
            skArc(sketch, "E156.filletArc", {"start": v(-129.94, 404.83) * mm, "mid": v(-138.58, 412.34) * mm, "end": v(-149.65, 415.28) * mm});
            skArc(sketch, "E157", {"start": v(-185.71, 493.4) * mm, "mid": v(-104.62, 398.3) * mm, "end": v(11.4, 351.8) * mm});
            skSolve(sketch);
        }
        {
            var Q0;
            Q0=makeQuery(id+"F24.imprint","IMPRINT",FACE,{"disambiguationData":[TD([[makeQuery(id+"F24.imprint","IMPRINT",EDGE,{"derivedFrom":sQuery(id+"F24.wireOp",EDGE,"E147")}),1.0]])]});
            var Q1;
            Q1=sQuery(id+"F24.wireOp",EDGE,"E150");
            revolve(context, id + "F25", {"entities" : qUnion([Q0]), "axis" : qUnion([Q1]), "revolveType" : RevolveType.FULL});
        }
        {
            var Q0;
            Q0=makeQuery(id+"F25.opRevolve","SWEPT_BODY",BODY,{"disambiguationData":[OSD([sQuery(id+"F24.wireOp",EDGE,"E147"),sQuery(id+"F24.wireOp",EDGE,"E148"),sQuery(id+"F24.wireOp",EDGE,"E149"),sQuery(id+"F24.wireOp",EDGE,"E150"),sQuery(id+"F24.wireOp",EDGE,"E151"),sQuery(id+"F24.wireOp",EDGE,"E152"),sQuery(id+"F24.wireOp",EDGE,"E154.filletArc"),sQuery(id+"F24.wireOp",EDGE,"E155.filletArc"),sQuery(id+"F24.wireOp",EDGE,"E156.filletArc"),sQuery(id+"F24.wireOp",EDGE,"E157")])]});
            transform(context, id + "F26", {"entities" : qUnion([Q0]), "transformType" : TransformType.TRANSLATION_3D, "dx" : -210.82 * mm, "dy" : 0 * mm, "dz" : 0 * mm, "makeCopy" : false});
        }
        {
            var Q0;
            Q0=makeQuery(id+"F14.opPattern","COPY",FACE,{"derivedFrom":makeQuery(id+"F13.opExtrude","CAP_FACE",FACE,{"disambiguationData":[OSD([sQuery(id+"F12.wireOp",EDGE,"E132.bottom"),sQuery(id+"F12.wireOp",EDGE,"E132.top"),sQuery(id+"F12.wireOp",EDGE,"E132.left"),sQuery(id+"F12.wireOp",EDGE,"E132.right")])],"isStart":false}),"instanceName":"1"});
            cPlane(context, id + "F27", {"entities" : qUnion([Q0]), "cplaneType" : CPlaneType.OFFSET, "offset" : 647.7 * mm, "oppositeDirection" : true, "width" : 152.4 * mm, "height" : 152.4 * mm});
        }
        {
            var Q0;
            Q0=makeQuery(id+"F25.opRevolve","SWEPT_BODY",BODY,{"disambiguationData":[OSD([sQuery(id+"F24.wireOp",EDGE,"E147"),sQuery(id+"F24.wireOp",EDGE,"E148"),sQuery(id+"F24.wireOp",EDGE,"E149"),sQuery(id+"F24.wireOp",EDGE,"E150"),sQuery(id+"F24.wireOp",EDGE,"E151"),sQuery(id+"F24.wireOp",EDGE,"E152"),sQuery(id+"F24.wireOp",EDGE,"E154.filletArc"),sQuery(id+"F24.wireOp",EDGE,"E155.filletArc"),sQuery(id+"F24.wireOp",EDGE,"E156.filletArc"),sQuery(id+"F24.wireOp",EDGE,"E157")])]});
            var Q1;
            Q1=qCreatedBy(id+"F27.planeOp",FACE);
            mirror(context, id + "F28", {"operationType" : NewBodyOperationType.ADD, "entities" : qUnion([Q0]), "mirrorPlane" : qUnion([Q1])});
        }
        {
            var Q0;
            Q0=makeQuery(id+"F10.opExtrude","SWEPT_FACE",FACE,{"disambiguationData":[OSD([sQuery(id+"F8.wireOp",EDGE,"E128.bottom")])]});
            cPlane(context, id + "F29", {"entities" : qUnion([Q0]), "cplaneType" : CPlaneType.OFFSET, "offset" : 0 * mm, "width" : 152.4 * mm, "height" : 152.4 * mm});
        }
        {
            var Q0;
            Q0=qCreatedBy(id+"F29.planeOp",FACE);
            var sketch = newSketch(context, id + "F30", { "sketchPlane" : qUnion([Q0])});
            skLineSegment(sketch, "E158.0.0", {"start": v(-439.29, 25.4) * mm, "end": v(-439.29, 533.4) * mm});
            skLineSegment(sketch, "E158.0.1", {"start": v(-439.29, 533.4) * mm, "end": v(-464.69, 533.4) * mm});
            skLineSegment(sketch, "E158.0.2", {"start": v(-464.69, 533.4) * mm, "end": v(-464.69, 25.4) * mm});
            skLineSegment(sketch, "E158.0.3", {"start": v(-464.69, 25.4) * mm, "end": v(-439.29, 25.4) * mm});
            skLineSegment(sketch, "E158.1.0", {"start": v(-413.89, 25.4) * mm, "end": v(-464.69, 25.4) * mm});
            skLineSegment(sketch, "E158.1.1", {"start": v(-464.69, 25.4) * mm, "end": v(-464.69, -25.4) * mm});
            skLineSegment(sketch, "E158.1.2", {"start": v(-464.69, -25.4) * mm, "end": v(-413.89, -25.4) * mm});
            skLineSegment(sketch, "E158.1.3", {"start": v(-413.89, -25.4) * mm, "end": v(-413.89, 25.4) * mm});
            skLineSegment(sketch, "E158.2.0", {"start": v(-413.89, -25.4) * mm, "end": v(779.91, -25.4) * mm});
            skLineSegment(sketch, "E158.2.1", {"start": v(779.91, -25.4) * mm, "end": v(779.91, 0) * mm});
            skLineSegment(sketch, "E158.2.2", {"start": v(779.91, 0) * mm, "end": v(-413.89, 0) * mm});
            skLineSegment(sketch, "E158.2.3", {"start": v(-413.89, 0) * mm, "end": v(-413.89, -25.4) * mm});
            skLineSegment(sketch, "E158.3.0", {"start": v(-413.89, 558.8) * mm, "end": v(779.91, 558.8) * mm});
            skLineSegment(sketch, "E158.3.1", {"start": v(779.91, 558.8) * mm, "end": v(779.91, 584.2) * mm});
            skLineSegment(sketch, "E158.3.2", {"start": v(779.91, 584.2) * mm, "end": v(-413.89, 584.2) * mm});
            skLineSegment(sketch, "E158.3.3", {"start": v(-413.89, 584.2) * mm, "end": v(-413.89, 558.8) * mm});
            skLineSegment(sketch, "E158.4.0", {"start": v(-413.89, 584.2) * mm, "end": v(-464.69, 584.2) * mm});
            skLineSegment(sketch, "E158.4.1", {"start": v(-464.69, 584.2) * mm, "end": v(-464.69, 533.4) * mm});
            skLineSegment(sketch, "E158.4.2", {"start": v(-464.69, 533.4) * mm, "end": v(-413.89, 533.4) * mm});
            skLineSegment(sketch, "E158.4.3", {"start": v(-413.89, 533.4) * mm, "end": v(-413.89, 584.2) * mm});
            skLineSegment(sketch, "E158.5.0", {"start": v(830.71, 25.4) * mm, "end": v(830.71, 533.4) * mm});
            skLineSegment(sketch, "E158.5.1", {"start": v(830.71, 533.4) * mm, "end": v(805.31, 533.4) * mm});
            skLineSegment(sketch, "E158.5.2", {"start": v(805.31, 533.4) * mm, "end": v(805.31, 25.4) * mm});
            skLineSegment(sketch, "E158.5.3", {"start": v(805.31, 25.4) * mm, "end": v(830.71, 25.4) * mm});
            skLineSegment(sketch, "E158.6.0", {"start": v(830.71, 25.4) * mm, "end": v(779.91, 25.4) * mm});
            skLineSegment(sketch, "E158.6.1", {"start": v(779.91, 25.4) * mm, "end": v(779.91, -25.4) * mm});
            skLineSegment(sketch, "E158.6.2", {"start": v(779.91, -25.4) * mm, "end": v(830.71, -25.4) * mm});
            skLineSegment(sketch, "E158.6.3", {"start": v(830.71, -25.4) * mm, "end": v(830.71, 25.4) * mm});
            skLineSegment(sketch, "E158.7.0", {"start": v(830.71, 584.2) * mm, "end": v(779.91, 584.2) * mm});
            skLineSegment(sketch, "E158.7.1", {"start": v(779.91, 584.2) * mm, "end": v(779.91, 533.4) * mm});
            skLineSegment(sketch, "E158.7.2", {"start": v(779.91, 533.4) * mm, "end": v(830.71, 533.4) * mm});
            skLineSegment(sketch, "E158.7.3", {"start": v(830.71, 533.4) * mm, "end": v(830.71, 584.2) * mm});
            skLineSegment(sketch, "E159.bottom", {"start": v(-464.69, 584.2) * mm, "end": v(830.71, 584.2) * mm});
            skLineSegment(sketch, "E159.top", {"start": v(-464.69, -25.4) * mm, "end": v(830.71, -25.4) * mm});
            skLineSegment(sketch, "E159.left", {"start": v(-464.69, 584.2) * mm, "end": v(-464.69, -25.4) * mm});
            skLineSegment(sketch, "E159.right", {"start": v(830.71, 584.2) * mm, "end": v(830.71, -25.4) * mm});
            skSolve(sketch);
        }
        {
            var Q0;
            {var subQ8=sQuery(id+"F30.wireOp",EDGE,"E158.0.0");Q0=makeQuery(id+"F30.imprint","IMPRINT",FACE,{"disambiguationData":[TD([[makeQuery(id+"F30.imprint","IMPRINT",EDGE,{"derivedFrom":subQ8}),-1.0]])]});}
            extrude(context, id + "F31", {"entities" : qUnion([Q0]), "oppositeDirection" : true, "depth" : 25.4 * mm, "offsetDistance" : 25.4 * mm});
        }
        {
            var Q0;
            Q0=makeQuery(id+"F16.opPattern","COPY",FACE,{"derivedFrom":makeQuery(id+"F13.opExtrude","SWEPT_FACE",FACE,{"disambiguationData":[OSD([sQuery(id+"F12.wireOp",EDGE,"E136.bottom")])]}),"instanceName":"1"});
            cPlane(context, id + "F32", {"entities" : qUnion([Q0]), "cplaneType" : CPlaneType.OFFSET, "offset" : 0 * mm, "width" : 152.4 * mm, "height" : 152.4 * mm});
        }
        {
            var Q0;
            Q0=qCreatedBy(id+"F32.planeOp",FACE);
            var sketch = newSketch(context, id + "F33", { "sketchPlane" : qUnion([Q0])});
            skLineSegment(sketch, "E160.0.0", {"start": v(-413.89, 584.2) * mm, "end": v(-464.69, 584.2) * mm});
            skLineSegment(sketch, "E160.0.1", {"start": v(-464.69, 584.2) * mm, "end": v(-464.69, 533.4) * mm});
            skLineSegment(sketch, "E160.0.2", {"start": v(-464.69, 533.4) * mm, "end": v(-413.89, 533.4) * mm});
            skLineSegment(sketch, "E160.0.3", {"start": v(-413.89, 533.4) * mm, "end": v(-413.89, 584.2) * mm});
            skLineSegment(sketch, "E160.1.0", {"start": v(-439.29, 25.4) * mm, "end": v(-439.29, 533.4) * mm});
            skLineSegment(sketch, "E160.1.1", {"start": v(-439.29, 533.4) * mm, "end": v(-464.69, 533.4) * mm});
            skLineSegment(sketch, "E160.1.2", {"start": v(-464.69, 533.4) * mm, "end": v(-464.69, 25.4) * mm});
            skLineSegment(sketch, "E160.1.3", {"start": v(-464.69, 25.4) * mm, "end": v(-439.29, 25.4) * mm});
            skLineSegment(sketch, "E160.2.0", {"start": v(-413.89, 25.4) * mm, "end": v(-464.69, 25.4) * mm});
            skLineSegment(sketch, "E160.2.1", {"start": v(-464.69, 25.4) * mm, "end": v(-464.69, -25.4) * mm});
            skLineSegment(sketch, "E160.2.2", {"start": v(-464.69, -25.4) * mm, "end": v(-413.89, -25.4) * mm});
            skLineSegment(sketch, "E160.2.3", {"start": v(-413.89, -25.4) * mm, "end": v(-413.89, 25.4) * mm});
            skLineSegment(sketch, "E160.3.0", {"start": v(-413.89, -25.4) * mm, "end": v(779.91, -25.4) * mm});
            skLineSegment(sketch, "E160.3.1", {"start": v(779.91, -25.4) * mm, "end": v(779.91, 0) * mm});
            skLineSegment(sketch, "E160.3.2", {"start": v(779.91, 0) * mm, "end": v(-413.89, 0) * mm});
            skLineSegment(sketch, "E160.3.3", {"start": v(-413.89, 0) * mm, "end": v(-413.89, -25.4) * mm});
            skLineSegment(sketch, "E160.4.0", {"start": v(-413.89, 558.8) * mm, "end": v(779.91, 558.8) * mm});
            skLineSegment(sketch, "E160.4.1", {"start": v(779.91, 558.8) * mm, "end": v(779.91, 584.2) * mm});
            skLineSegment(sketch, "E160.4.2", {"start": v(779.91, 584.2) * mm, "end": v(-413.89, 584.2) * mm});
            skLineSegment(sketch, "E160.4.3", {"start": v(-413.89, 584.2) * mm, "end": v(-413.89, 558.8) * mm});
            skLineSegment(sketch, "E160.5.0", {"start": v(830.71, 584.2) * mm, "end": v(779.91, 584.2) * mm});
            skLineSegment(sketch, "E160.5.1", {"start": v(779.91, 584.2) * mm, "end": v(779.91, 533.4) * mm});
            skLineSegment(sketch, "E160.5.2", {"start": v(779.91, 533.4) * mm, "end": v(830.71, 533.4) * mm});
            skLineSegment(sketch, "E160.5.3", {"start": v(830.71, 533.4) * mm, "end": v(830.71, 584.2) * mm});
            skLineSegment(sketch, "E160.6.0", {"start": v(830.71, 25.4) * mm, "end": v(830.71, 533.4) * mm});
            skLineSegment(sketch, "E160.6.1", {"start": v(830.71, 533.4) * mm, "end": v(805.31, 533.4) * mm});
            skLineSegment(sketch, "E160.6.2", {"start": v(805.31, 533.4) * mm, "end": v(805.31, 25.4) * mm});
            skLineSegment(sketch, "E160.6.3", {"start": v(805.31, 25.4) * mm, "end": v(830.71, 25.4) * mm});
            skLineSegment(sketch, "E160.7.0", {"start": v(830.71, 25.4) * mm, "end": v(779.91, 25.4) * mm});
            skLineSegment(sketch, "E160.7.1", {"start": v(779.91, 25.4) * mm, "end": v(779.91, -25.4) * mm});
            skLineSegment(sketch, "E160.7.2", {"start": v(779.91, -25.4) * mm, "end": v(830.71, -25.4) * mm});
            skLineSegment(sketch, "E160.7.3", {"start": v(830.71, -25.4) * mm, "end": v(830.71, 25.4) * mm});
            skLineSegment(sketch, "E161.bottom", {"start": v(-464.69, 584.2) * mm, "end": v(830.71, 584.2) * mm});
            skLineSegment(sketch, "E161.top", {"start": v(-464.69, -25.4) * mm, "end": v(830.71, -25.4) * mm});
            skLineSegment(sketch, "E161.left", {"start": v(-464.69, 584.2) * mm, "end": v(-464.69, -25.4) * mm});
            skLineSegment(sketch, "E161.right", {"start": v(830.71, 584.2) * mm, "end": v(830.71, -25.4) * mm});
            skSolve(sketch);
        }
        {
            var Q0;
            Q0=makeQuery(id+"F33.imprint","IMPRINT",FACE,{"disambiguationData":[TD([[makeQuery(id+"F33.imprint","IMPRINT",EDGE,{"derivedFrom":sQuery(id+"F33.wireOp",EDGE,"E160.0.2")}),-1.0]])]});
            extrude(context, id + "F34", {"entities" : qUnion([Q0]), "oppositeDirection" : true, "depth" : 25.4 * mm, "offsetDistance" : 25.4 * mm});
        }
    });
